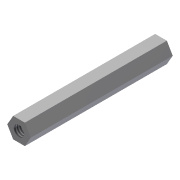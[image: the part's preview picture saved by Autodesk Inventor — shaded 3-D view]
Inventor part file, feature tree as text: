
AUTODESK INVENTOR PART (.ipt)
format: ipt  version: 2013 (Build 170138000, 138)  size: 80,384 bytes
history: native  units: in
note: dims shown in document units (in); Inventor stores cm internally (conversion verified against a paired STEP export)
features: sketch x2, extrude x1, hole x1, mirror x1
ambient origin geometry x8: Origin, YZ Plane, XZ Plane, XY Plane, X Axis, Y Axis, Z Axis, Center Point
bodies: Solid1 (feature_tree)
feature tree (5):
  extrude  "Extrusion1"  Depth=1.75in TaperAngle=0.0deg
  hole  "Hole1"  [1 undecoded]
  mirror  "Mirror1"
  sketch  "Sketch1"  dims[d0=0.25in d1=1.75in d2=0.0in]
  sketch  "Sketch2"  dims[d3=0.13in d4=0.375in d5=0.375in d6=0.25in d7=0.5635in d8=0.375in d9=0.0in]
note: 1 required parameter value undecoded (feature->parameter linkage not recoverable at this tier; creation-order binding heuristic only, values carry confidence <= 0.55)
